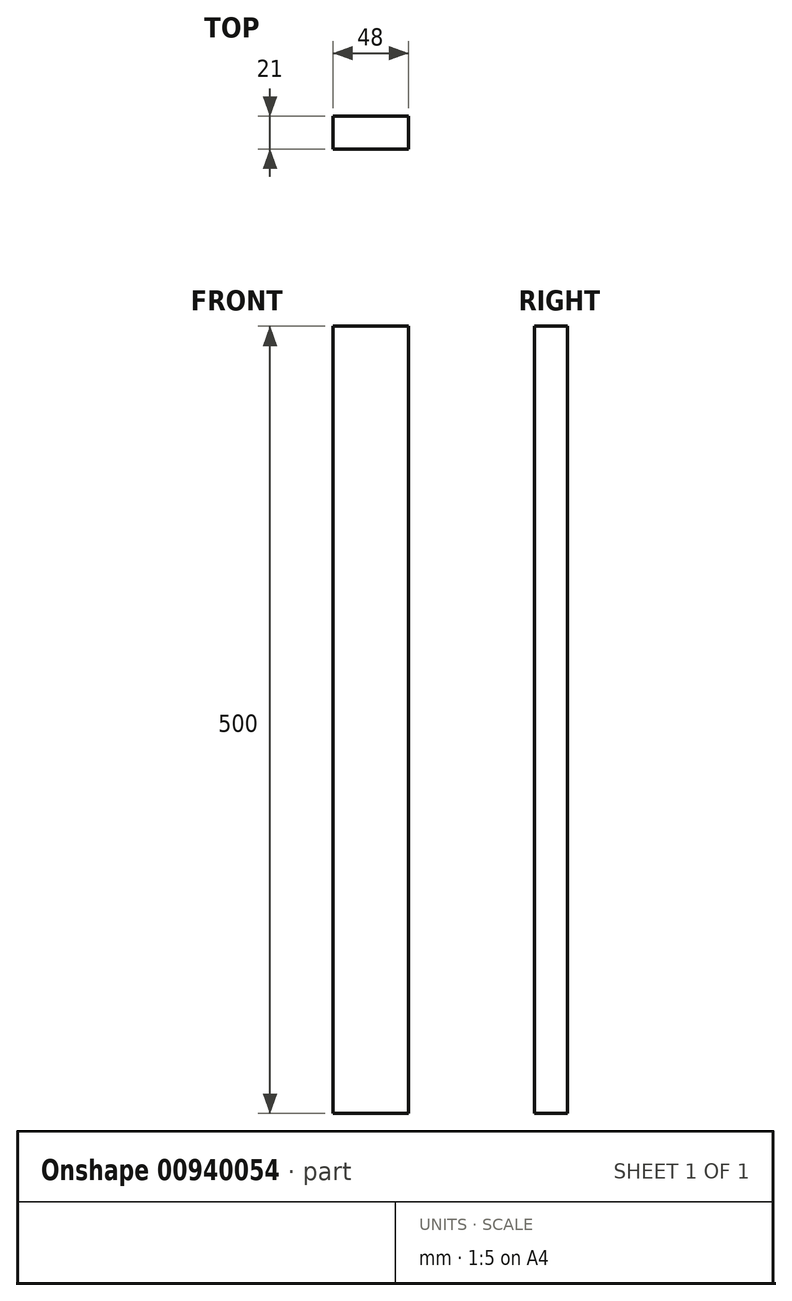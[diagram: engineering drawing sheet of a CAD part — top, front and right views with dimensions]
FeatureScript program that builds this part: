
annotation { "Feature Type Name" : "Feature", "Feature Type Description" : "" }
export const myFeature = defineFeature(function(context is Context, id is Id, definition is map)
    precondition{}
    {
        {
            var Q0;
            Q0=qCreatedBy(makeId("Top.planeOp"),FACE);
            var sketch = newSketch(context, id + "F0", { "sketchPlane" : qUnion([Q0])});
            skLineSegment(sketch, "E0.bottom", {"start": v(24, 10.5) * mm, "end": v(-24, 10.5) * mm});
            skLineSegment(sketch, "E0.top", {"start": v(24, -10.5) * mm, "end": v(-24, -10.5) * mm});
            skLineSegment(sketch, "E0.left", {"start": v(24, 10.5) * mm, "end": v(24, -10.5) * mm});
            skLineSegment(sketch, "E0.right", {"start": v(-24, 10.5) * mm, "end": v(-24, -10.5) * mm});
            skPoint(sketch, "E0.middle", {"position": v(0, 0) * mm});
            skSolve(sketch);
        }
        {
            var Q0;
            Q0 = qSketchRegion(id + "F0", true);
            extrude(context, id + "F1", {"entities" : qUnion([Q0]), "depth" : 500 * mm, "offsetDistance" : 25 * mm});
        }
    });
